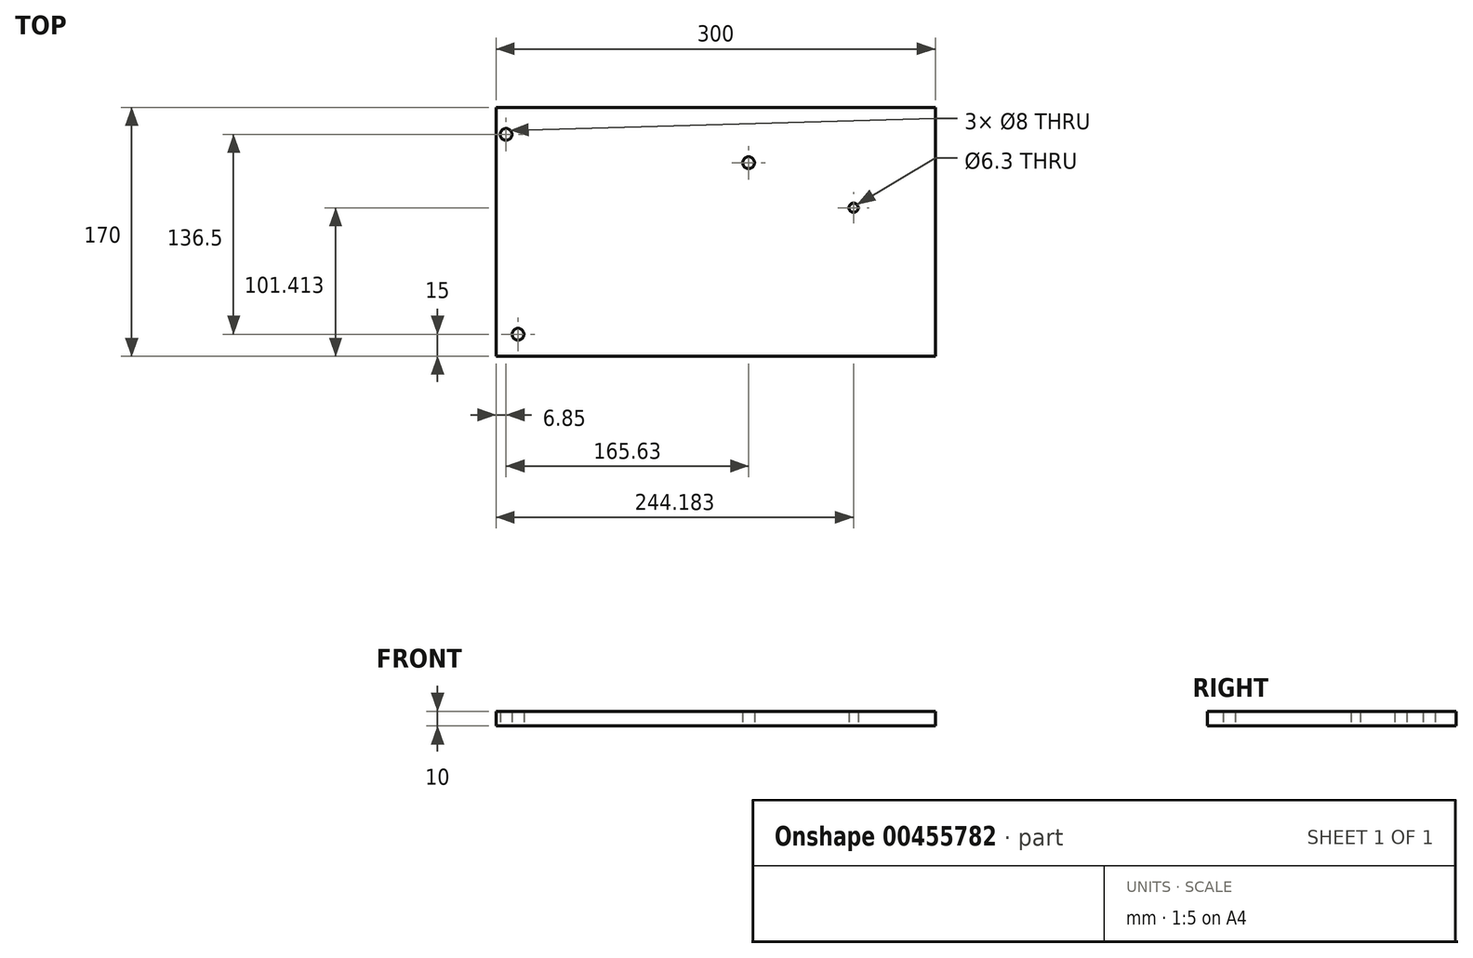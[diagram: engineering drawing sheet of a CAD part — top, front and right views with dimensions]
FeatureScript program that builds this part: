
annotation { "Feature Type Name" : "Feature", "Feature Type Description" : "" }
export const myFeature = defineFeature(function(context is Context, id is Id, definition is map)
    precondition{}
    {
        {
            var Q0;
            Q0=qCreatedBy(makeId("Top.planeOp"),FACE);
            var sketch = newSketch(context, id + "F0", { "sketchPlane" : qUnion([Q0])});
            skLineSegment(sketch, "E0.bottom", {"start": v(0, 0) * mm, "end": v(-300, 0) * mm});
            skLineSegment(sketch, "E0.top", {"start": v(0, -170) * mm, "end": v(-300, -170) * mm});
            skLineSegment(sketch, "E0.left", {"start": v(0, 0) * mm, "end": v(0, -170) * mm});
            skLineSegment(sketch, "E0.right", {"start": v(-300, 0) * mm, "end": v(-300, -170) * mm});
            skCircle(sketch, "E1", {"center": v(-285, -155) * mm, "radius": 4 * mm});
            skCircle(sketch, "E2", {"center": v(-293.15, -18.5) * mm, "radius": 4 * mm});
            skCircle(sketch, "E3", {"center": v(-127.52, -37.86) * mm, "radius": 4 * mm});
            skSolve(sketch);
        }
        {
            var Q0;
            Q0 = qSketchRegion(id + "F0", true);
            extrude(context, id + "F1", {"entities" : qUnion([Q0]), "depth" : 10 * mm});
        }
        {
            var Q0;
            Q0=qCreatedBy(makeId("Top.planeOp"),FACE);
            var sketch = newSketch(context, id + "F2", { "sketchPlane" : qUnion([Q0])});
            skCircle(sketch, "E4", {"center": v(-55.82, -68.59) * mm, "radius": 4.05 * mm});
            skSolve(sketch);
        }
        {
            var Q0;
            Q0=sQuery(id+"F2.wireOp",VERTEX,"E4.center");
            var Q1;
            Q1=makeQuery(id+"F1.opExtrude","SWEPT_BODY",BODY,{"disambiguationData":[OSD([sQuery(id+"F0.wireOp",EDGE,"E0.bottom"),sQuery(id+"F0.wireOp",EDGE,"E0.top"),sQuery(id+"F0.wireOp",EDGE,"E0.left"),sQuery(id+"F0.wireOp",EDGE,"E0.right")])]});
            hole(context, id + "F3", {"style" : HoleStyle.SIMPLE, "endStyle" : HoleEndStyle.THROUGH, "oppositeDirection" : true, "standardTappedOrClearance" : lookupTablePath({ "standard" : "ISO", "fit" : "Close", "size" : "M6", "type" : "Clearance" }), "standardBlindInLast" : lookupTablePath({ "fit" : "Close", "standard" : "ISO", "size" : "M6", "type" : "Clearance" }), "holeDiameter" : 6.3 * mm, "isTappedThrough" : true, "tappedDepth" : 12 * mm, "tapClearance" : 3, "locations" : qUnion([Q0]), "scope" : qUnion([Q1])});
        }
    });
